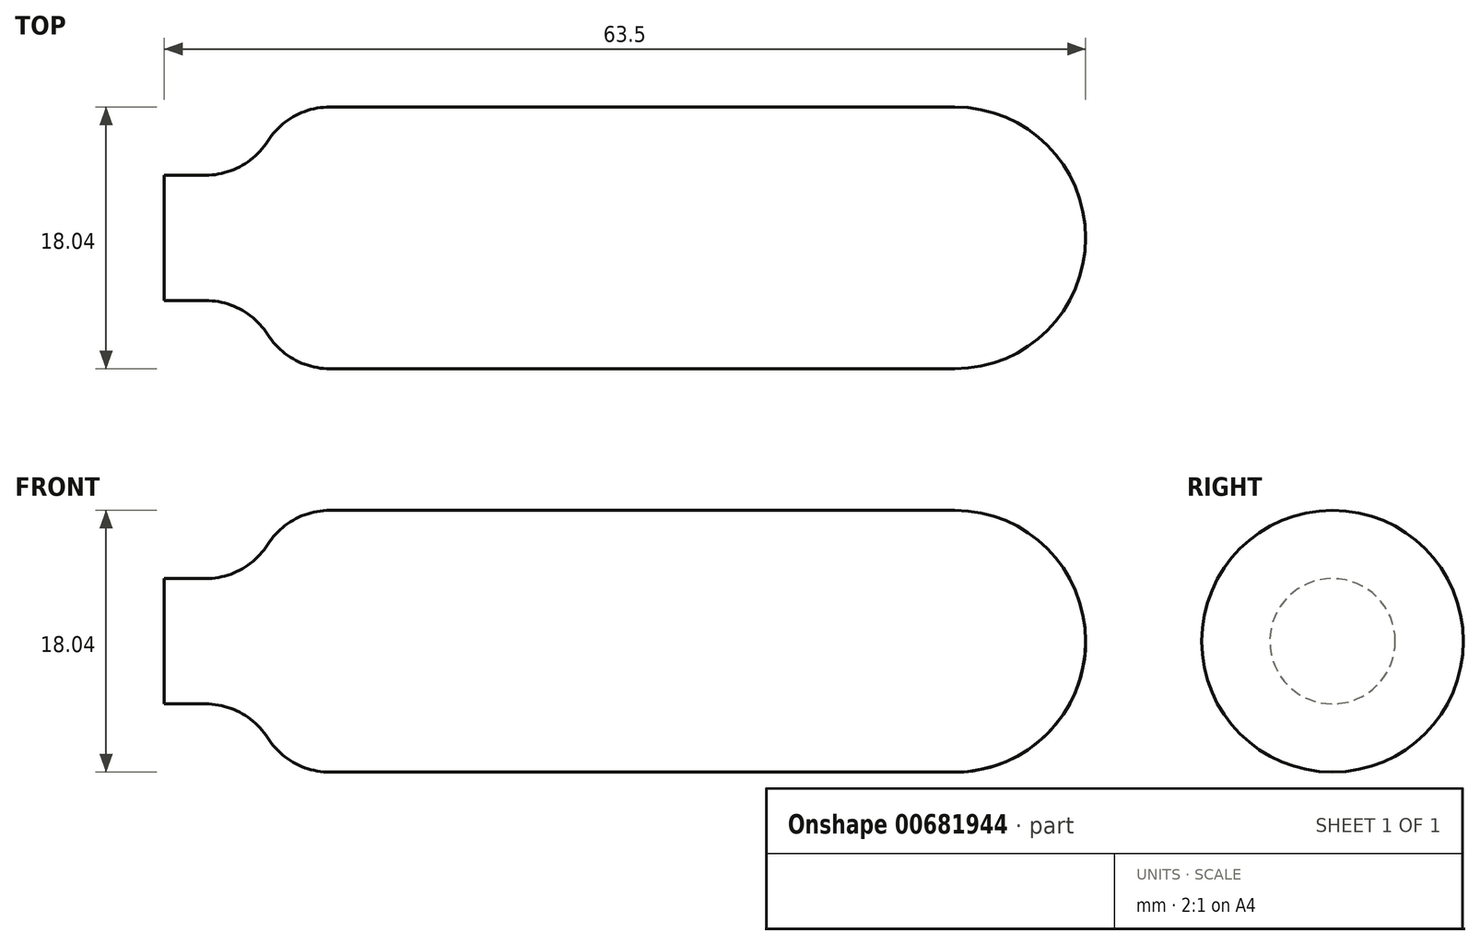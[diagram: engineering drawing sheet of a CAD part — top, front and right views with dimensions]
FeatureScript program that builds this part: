
annotation { "Feature Type Name" : "Feature", "Feature Type Description" : "" }
export const myFeature = defineFeature(function(context is Context, id is Id, definition is map)
    precondition{}
    {
        {
            var Q0;
            Q0=qCreatedBy(makeId("Right.planeOp"),FACE);
            var sketch = newSketch(context, id + "F0", { "sketchPlane" : qUnion([Q0])});
            skCircle(sketch, "E0", {"center": v(0, 0) * mm, "radius": 9.02 * mm});
            skSolve(sketch);
        }
        {
            var Q0;
            Q0 = qSketchRegion(id + "F0", true);
            extrude(context, id + "F1", {"entities" : qUnion([Q0]), "depth" : 57.15 * mm, "offsetDistance" : 25.4 * mm});
        }
        {
            var Q0;
            Q0=makeQuery(id+"F1.opExtrude","CAP_FACE",FACE,{"disambiguationData":[OSD([sQuery(id+"F0.wireOp",EDGE,"E0")])],"isStart":true});
            var sketch = newSketch(context, id + "F2", { "sketchPlane" : qUnion([Q0])});
            skCircle(sketch, "E1", {"center": v(0, 0) * mm, "radius": 4.32 * mm});
            skSolve(sketch);
        }
        {
            var Q0;
            Q0 = qSketchRegion(id + "F2", true);
            extrude(context, id + "F3", {"entities" : qUnion([Q0]), "operationType" : NewBodyOperationType.ADD, "depth" : 6.35 * mm, "offsetDistance" : 25.4 * mm});
        }
        {
            var Q0;
            Q0=makeQuery(id+"F3.opExtrude","CAP_FACE",FACE,{"disambiguationData":[OSD([sQuery(id+"F2.wireOp",EDGE,"E1")])],"isStart":false});
            var sketch = newSketch(context, id + "F4", { "sketchPlane" : qUnion([Q0])});
            skCircle(sketch, "E2", {"center": v(0, 0) * mm, "radius": 1.27 * mm});
            skSolve(sketch);
        }
        {
            var Q0;
            Q0=makeQuery(id+"F1.opExtrude","CAP_FACE",FACE,{"disambiguationData":[OSD([sQuery(id+"F0.wireOp",EDGE,"E0")])],"isStart":false});
            fillet(context, id + "F5", {"entities" : qUnion([Q0]), "radius" : 9.02 * mm, "tangentPropagation" : true, "allowEdgeOverflow" : false});
        }
        {
            var Q0;
            Q0=makeQuery(id+"F1.opExtrude","SWEPT_FACE",FACE,{"disambiguationData":[OSD([sQuery(id+"F0.wireOp",EDGE,"E0")])]});
            fillet(context, id + "F6", {"entities" : qUnion([Q0]), "radius" : 5.08 * mm, "tangentPropagation" : true, "allowEdgeOverflow" : false});
        }
        {
            var Q0;
            Q0=makeQuery(id+"F6.opFillet","BLEND_EDGE",EDGE,{"blendedFrom":[makeQuery(id+"F1.opExtrude","CAP_EDGE",EDGE,{"disambiguationData":[OSD([sQuery(id+"F0.wireOp",EDGE,"E0")])],"isStart":true}),makeQuery(id+"F3.opExtrude","SWEPT_FACE",FACE,{"disambiguationData":[OSD([sQuery(id+"F2.wireOp",EDGE,"E1")])]})],"blendedInto":[makeQuery(id+"F3.opExtrude","SWEPT_FACE",FACE,{"disambiguationData":[OSD([sQuery(id+"F2.wireOp",EDGE,"E1")])]})]});
            fillet(context, id + "F7", {"entities" : qUnion([Q0]), "radius" : 5.08 * mm, "tangentPropagation" : true, "allowEdgeOverflow" : false});
        }
    });
